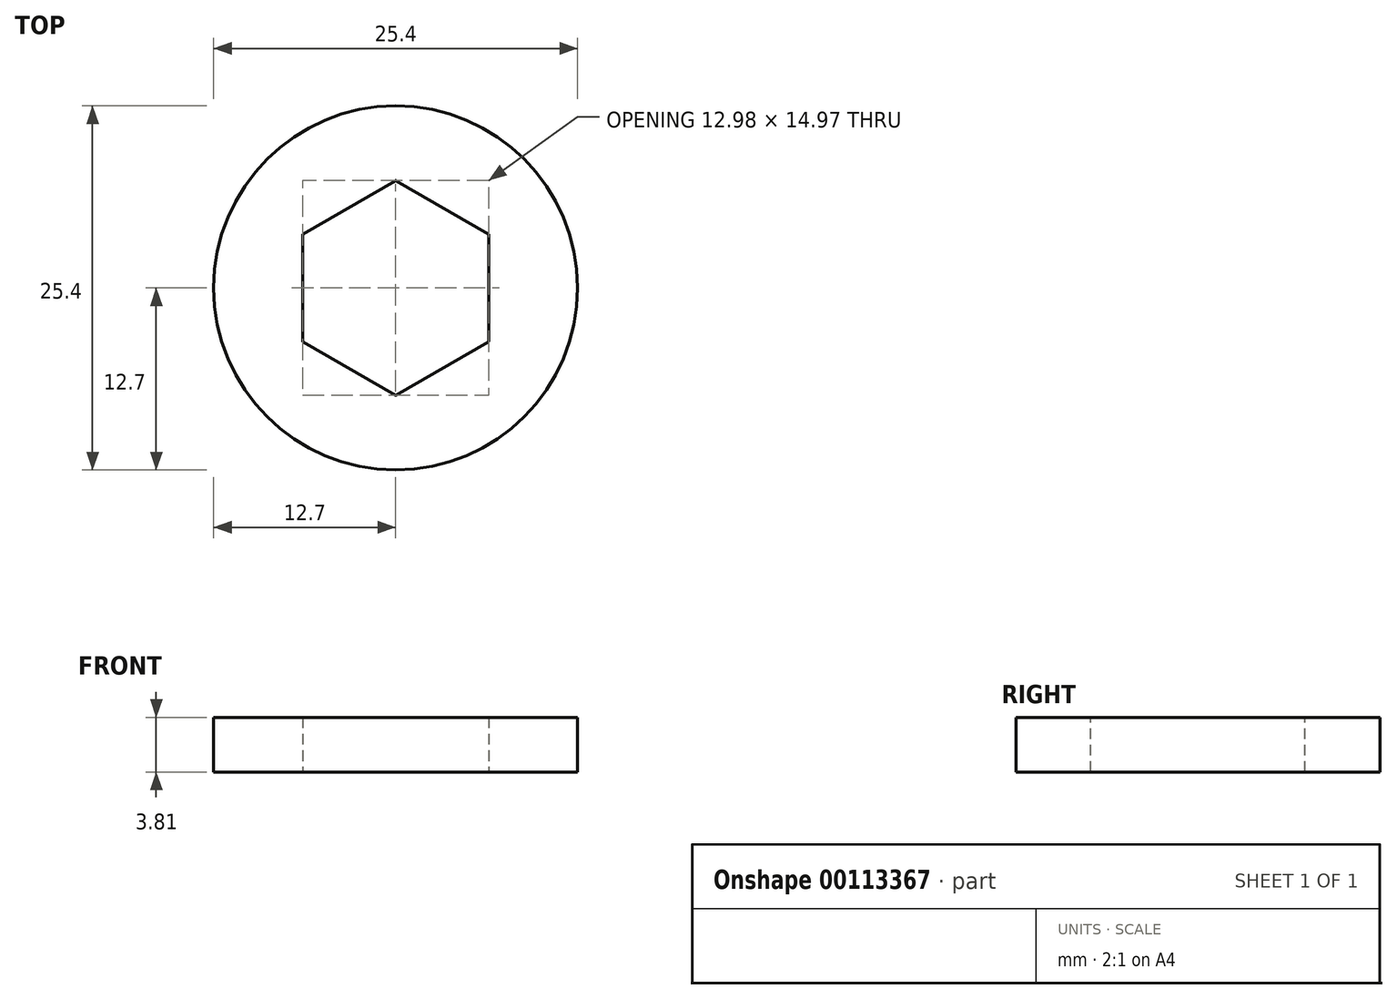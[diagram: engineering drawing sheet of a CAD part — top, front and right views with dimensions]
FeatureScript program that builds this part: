
annotation { "Feature Type Name" : "Feature", "Feature Type Description" : "" }
export const myFeature = defineFeature(function(context is Context, id is Id, definition is map)
    precondition{}
    {
        {
            var Q0;
            Q0=qCreatedBy(makeId("Top.planeOp"),FACE);
            var sketch = newSketch(context, id + "F0", { "sketchPlane" : qUnion([Q0])});
            skCircle(sketch, "E0", {"center": v(0, 0) * mm, "radius": 12.7 * mm});
            skCircle(sketch, "E1.cCircle", {"center": v(0, 0) * mm, "radius": 6.49 * mm, "construction": true});
            skLineSegment(sketch, "E1.0", {"start": v(6.49, 3.75) * mm, "end": v(6.49, -3.75) * mm});
            skLineSegment(sketch, "E1.1", {"start": v(6.49, -3.75) * mm, "end": v(0, -7.5) * mm});
            skLineSegment(sketch, "E1.2", {"start": v(0, -7.5) * mm, "end": v(-6.49, -3.75) * mm});
            skLineSegment(sketch, "E1.3", {"start": v(-6.49, -3.75) * mm, "end": v(-6.49, 3.75) * mm});
            skLineSegment(sketch, "E1.4", {"start": v(-6.49, 3.75) * mm, "end": v(0, 7.5) * mm});
            skLineSegment(sketch, "E1.5", {"start": v(0, 7.5) * mm, "end": v(6.49, 3.75) * mm});
            skPoint(sketch, "E1.0.midPoint", {"position": v(6.49, 0) * mm});
            skSolve(sketch);
        }
        {
            var Q0;
            Q0 = qSketchRegion(id + "F0", true);
            extrude(context, id + "F1", {"entities" : qUnion([Q0]), "depth" : 3.8 * mm, "offsetDistance" : 25.4 * mm});
        }
        {
            var Q0;
            Q0=makeQuery(id+"F1.opExtrude","SWEPT_EDGE",EDGE,{"disambiguationData":[OSD([sQuery(id+"F0.wireOp",EDGE,"E1.2"),sQuery(id+"F0.wireOp",EDGE,"E1.3")])]});
            var Q1;
            Q1=makeQuery(id+"F1.opExtrude","SWEPT_EDGE",EDGE,{"disambiguationData":[OSD([sQuery(id+"F0.wireOp",EDGE,"E1.3"),sQuery(id+"F0.wireOp",EDGE,"E1.4")])]});
            var Q2;
            Q2=makeQuery(id+"F1.opExtrude","SWEPT_EDGE",EDGE,{"disambiguationData":[OSD([sQuery(id+"F0.wireOp",EDGE,"E1.4"),sQuery(id+"F0.wireOp",EDGE,"E1.5")])]});
            var Q3;
            Q3=makeQuery(id+"F1.opExtrude","SWEPT_EDGE",EDGE,{"disambiguationData":[OSD([sQuery(id+"F0.wireOp",EDGE,"E1.0"),sQuery(id+"F0.wireOp",EDGE,"E1.5")])]});
            var Q4;
            Q4=makeQuery(id+"F1.opExtrude","SWEPT_EDGE",EDGE,{"disambiguationData":[OSD([sQuery(id+"F0.wireOp",EDGE,"E1.0"),sQuery(id+"F0.wireOp",EDGE,"E1.1")])]});
            var Q5;
            Q5=makeQuery(id+"F1.opExtrude","SWEPT_EDGE",EDGE,{"disambiguationData":[OSD([sQuery(id+"F0.wireOp",EDGE,"E1.1"),sQuery(id+"F0.wireOp",EDGE,"E1.2")])]});
            fillet(context, id + "F2", {"entities" : qUnion([Q0, Q1, Q2, Q3, Q4, Q5]), "tangentPropagation" : true, "radius" : 0.05 * mm, "defaultsChanged" : true, "vertexSettings" : [], "allowEdgeOverflow" : false});
        }
    });
